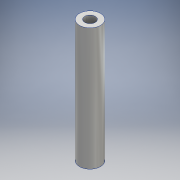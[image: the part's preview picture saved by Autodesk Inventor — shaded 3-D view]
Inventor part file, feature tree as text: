
AUTODESK INVENTOR PART (.ipt)
format: ipt  version: 2020.2 (Build 242310000, 310)  size: 106,496 bytes
history: native  units: mm
features: sketch x2, extrude x2, hole x2, other x1
ambient origin geometry x8: Origin, YZ Plane, XZ Plane, XY Plane, X Axis, Y Axis, Z Axis, Center Point
bodies: Body1 (feature_tree)
feature tree (7):
  other  "ソリッド1"
  sketch  "スケッチ1"
  extrude  "押し出し1"  Depth=6.0mm
  sketch  "スケッチ2"
  extrude  "押し出し2"  Depth=3.001mm
  hole  "穴1"  [1 undecoded]
  hole  "穴2"  [1 undecoded]
note: 2 required parameter values undecoded (feature->parameter linkage not recoverable at this tier; creation-order binding heuristic only, values carry confidence <= 0.55)
